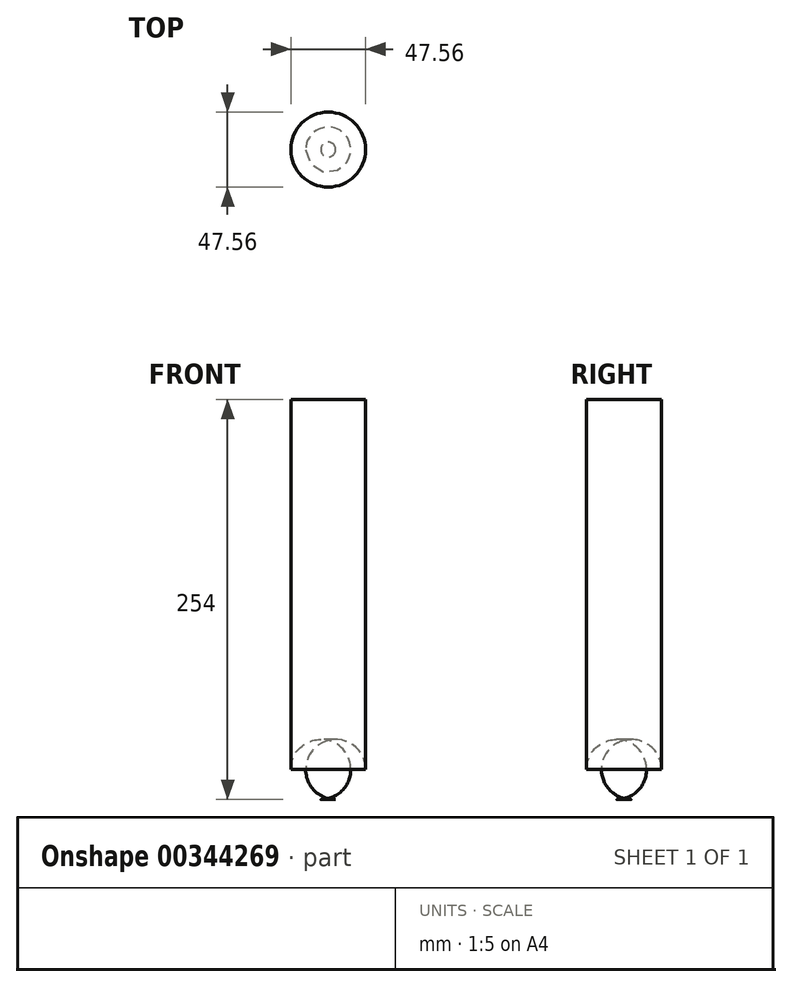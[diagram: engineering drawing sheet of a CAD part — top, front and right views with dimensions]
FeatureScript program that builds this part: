
annotation { "Feature Type Name" : "Feature", "Feature Type Description" : "" }
export const myFeature = defineFeature(function(context is Context, id is Id, definition is map)
    precondition{}
    {
        {
            var Q0;
            Q0=qCreatedBy(makeId("Top.planeOp"),FACE);
            var sketch = newSketch(context, id + "F0", { "sketchPlane" : qUnion([Q0])});
            skCircle(sketch, "E0", {"center": v(0, 0) * mm, "radius": 23.78 * mm});
            skSolve(sketch);
        }
        {
            var Q0;
            Q0=makeQuery(id+"F0.imprint","IMPRINT",FACE,{"disambiguationData":[TD([[makeQuery(id+"F0.imprint","IMPRINT",EDGE,{"derivedFrom":sQuery(id+"F0.wireOp",EDGE,"E0")}),1.0]])]});
            extrude(context, id + "F1", {"entities" : qUnion([Q0]), "depth" : 25.4 * mm, "hasSecondDirection" : true, "secondDirectionOppositeDirection" : true, "secondDirectionDepth" : 228.6 * mm});
        }
        {
            var Q0;
            Q0=makeQuery(id+"F1.opExtrude","CAP_FACE",FACE,{"disambiguationData":[OSD([sQuery(id+"F0.wireOp",EDGE,"E0")])],"isStart":true});
            fillet(context, id + "F2", {"entities" : qUnion([Q0]), "radius" : 19.05 * mm, "tangentPropagation" : true, "allowEdgeOverflow" : false});
        }
    });
